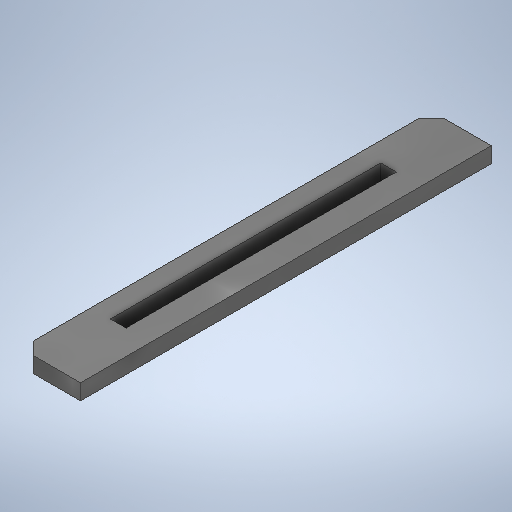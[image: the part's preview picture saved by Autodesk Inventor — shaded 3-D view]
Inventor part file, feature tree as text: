
AUTODESK INVENTOR PART (.ipt)
format: ipt  version: 2025 (Build 290162000, 162)  size: 262,656 bytes
history: native  units: in
note: dims shown in document units (in); Inventor stores cm internally (conversion verified against a paired STEP export)
features: extrude x3, sketch x3
ambient origin geometry x8: Origin, YZ Plane, XZ Plane, XY Plane, X Axis, Y Axis, Z Axis, Center Point
bodies: Solid1 (feature_tree)
feature tree (6):
  extrude  "Extrusion1"  Depth=0.0236in TaperAngle=0.0deg
  extrude  "Extrusion2"  Depth=0.4094in
  extrude  "Extrusion3"  Depth=0.0413in
  sketch  "Sketch1"  dims[d0=0.622in d1=0.0236in d2=0.0in]
  sketch  "Sketch2"  dims[d3=0.0236in d4=0.4094in]
  sketch  "Sketch3"  dims[d5=0.0in d6=0.0in d7=0.0413in d8=0.0492in d9=0.0197in d10=0.0197in d11=0.0197in d12=0.0197in d13=0.0in d14=0.0in d15=0.311in]
